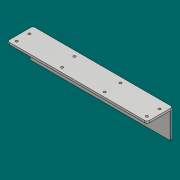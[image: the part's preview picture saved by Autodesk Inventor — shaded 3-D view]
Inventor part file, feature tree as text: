
AUTODESK INVENTOR PART (.ipt)
format: ipt  version: 2018 (Build 220112000, 112)  size: 125,952 bytes
history: native  units: mm
features: fillet x3, extrude x2, sketch x2, other x1
ambient origin geometry x8: Origin, YZ Plane, XZ Plane, XY Plane, X Axis, Y Axis, Z Axis, Center Point
bodies: Body1 (feature_tree)
feature tree (8):
  other  "ソリッド1"
  extrude  "押し出し1"  Depth=23.55mm
  extrude  "押し出し2"  Depth=84.0mm
  fillet  "フィレット1"  Radius=79.0mm
  fillet  "フィレット2"  Radius=78.0mm
  fillet  "フィレット3"  Radius=4.5mm
  sketch  "スケッチ1"
  sketch  "スケッチ2"
